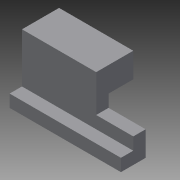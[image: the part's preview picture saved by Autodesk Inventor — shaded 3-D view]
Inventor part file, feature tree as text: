
AUTODESK INVENTOR PART (.ipt)
format: ipt  version: 2015 (Build 190159000, 159)  size: 95,744 bytes
history: native  units: in
note: dims shown in document units (in); Inventor stores cm internally (conversion verified against a paired STEP export)
features: extrude x3, sketch x3
ambient origin geometry x8: Origin, YZ Plane, XZ Plane, XY Plane, X Axis, Y Axis, Z Axis, Center Point
bodies: Solid1 (feature_tree)
feature tree (6):
  extrude  "Extrusion1"  Depth=4.5in
  extrude  "Extrusion2"  Depth=3.0in
  extrude  "Extrusion3"  Depth=4.5in
  sketch  "Sketch1"  dims[d0=2.5in d1=4.5in]
  sketch  "Sketch2"  dims[d2=1.0in d3=3.0in]
  sketch  "Sketch3"  dims[d4=1.5in d5=0.0in d6=4.5in d7=0.5in d8=0.5in d9=0.0in d10=1.0in d11=1.5in d12=5.9375in d13=0.0in]
